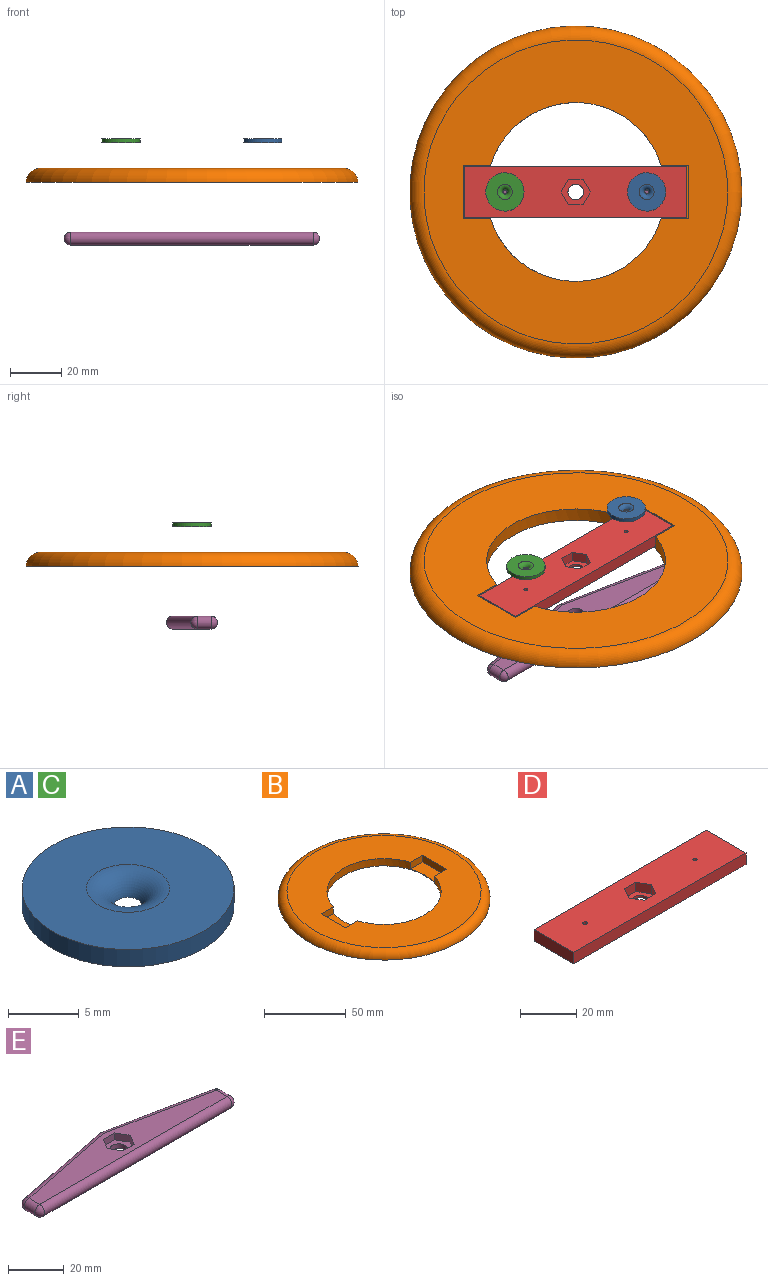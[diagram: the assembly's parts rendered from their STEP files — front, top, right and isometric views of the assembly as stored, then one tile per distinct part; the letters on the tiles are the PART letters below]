
ASSEMBLY  parts=5 mates=4
PART A: 4 faces, bbox 15x15x2 mm
  f0: cylinder r=7.5mm len=15mm, axis (0,0,-1), area 70.7mm2, adj f1,f2
  f1: plane 15x15mm, normal (0,0,1), area 149.6mm2, adj f0,f3
  f2: plane 15x15mm, normal (0,0,-1), area 173.6mm2, adj f0,f3
  f3: torus R=2.94mm, axis (0,0,1), area 29.8mm2, adj f1,f2
PART B: 12 faces, bbox 140.7x140.7x5.5 mm
  f0: plane 21x5mm, normal (1,0,0), area 105mm2, adj f1,f6,f7,f11
  f1: plane 10.61x5mm, normal (0,-1,0), area 53.1mm2, adj f0,f5,f7,f11
  f2: plane 10.61x5mm, normal (0,-1,0), area 53.1mm2, adj f3,f5,f7,f10
  f3: plane 21x5mm, normal (-1,0,0), area 105mm2, adj f2,f4,f7,f10
  f4: plane 10.61x5mm, normal (0,1,0), area 53.1mm2, adj f3,f5,f7,f10
  f5: cylinder r=35mm len=70mm, axis (0,0,-1), area 996.2mm2, adj f1,f2,f4,f6,f7,f8,f10,f11
  f6: plane 10.61x5mm, normal (0,1,0), area 53.1mm2, adj f0,f5,f7,f11
  f7: plane 119x119mm, normal (0,0,1), area 6873.2mm2, adj f0,f1,f2,f3,f4,f5,f6,f9
  f8: plane 130x130mm, normal (0,0,-1), area 9424.8mm2, adj f5,f9
  f9: torus R=59.5mm, axis (0,0,1), area 3419.9mm2, adj f7,f8
  f10: plane 21x10.61mm, normal (0,0,1), area 200.2mm2, adj f2,f3,f4,f5
  f11: plane 21x10.61mm, normal (0,0,1), area 200.2mm2, adj f0,f1,f5,f6
PART C: same geometry as A
PART D: 16 faces, bbox 87x20x5 mm
  f0: plane 87x5mm, normal (0,1,0), area 435mm2, adj f1,f11,f12,f13
  f1: plane 20x5mm, normal (-1,0,0), area 100mm2, adj f0,f2,f12,f13
  f2: plane 87x5mm, normal (0,-1,0), area 435mm2, adj f1,f11,f12,f13
  f3: plane 5x4mm, normal (-0.87,-0.5,0), area 23.1mm2, adj f4,f10,f12,f15
  f4: plane 5x4mm, normal (-0.87,0.5,0), area 23.1mm2, adj f3,f5,f12,f15
  f5: plane 5.77x4mm, normal (0,1,0), area 23.1mm2, adj f4,f6,f12,f15
  f6: plane 5x4mm, normal (0.87,0.5,0), area 23.1mm2, adj f5,f7,f12,f15
  f7: plane 5x4mm, normal (0.87,-0.5,0), area 23.1mm2, adj f6,f10,f12,f15
  f8: cylinder r=0.75mm len=5mm, axis (0,0,-1), area 23.6mm2, adj f12,f13
  f9: cylinder r=0.75mm len=5mm, axis (0,0,-1), area 23.6mm2, adj f12,f13
  f10: plane 5.77x4mm, normal (0,-1,0), area 23.1mm2, adj f3,f7,f12,f15
  f11: plane 20x5mm, normal (1,0,0), area 100mm2, adj f0,f2,f12,f13
  f12: plane 87x20mm, normal (0,0,1), area 1649.9mm2, adj f0,f1,f2,f3,f4,f5,f6,f7
  f13: plane 87x20mm, normal (0,0,-1), area 1707.2mm2, adj f0,f1,f2,f8,f9,f11,f14
  f14: cylinder r=3.05mm len=6.1mm, axis (0,0,-1), area 19.2mm2, adj f13,f15
  f15: plane 11.55x10mm, normal (0,0,1), area 57.4mm2, adj f3,f4,f5,f6,f7,f10,f14
PART E: 20 faces, bbox 100x20x5 mm
  f0: plane 5x3mm, normal (0.87,0.5,0), area 17.3mm2, adj f1,f5,f6,f9
  f1: plane 5x3mm, normal (0.87,-0.5,0), area 17.3mm2, adj f0,f2,f6,f9
  f2: plane 5.77x3mm, normal (0,-1,0), area 17.3mm2, adj f1,f3,f6,f9
  f3: plane 5x3mm, normal (-0.87,-0.5,0), area 17.3mm2, adj f2,f4,f6,f9
  f4: plane 5x3mm, normal (-0.87,0.5,0), area 17.3mm2, adj f3,f5,f6,f9
  f5: plane 5.77x3mm, normal (0,1,0), area 17.3mm2, adj f0,f4,f6,f9
  f6: plane 95x14.95mm, normal (0,0,1), area 882.4mm2, adj f0,f1,f2,f3,f4,f5,f10,f13
  f7: plane 95x14.95mm, normal (0,0,-1), area 939.8mm2, adj f8,f10,f13,f14,f17,f18
  f8: cylinder r=3.05mm len=6.1mm, axis (0,0,-1), area 38.3mm2, adj f7,f9
  f9: plane 11.55x10mm, normal (0,0,1), area 57.4mm2, adj f0,f1,f2,f3,f4,f5,f8
  f10: cylinder r=2.5mm len=95mm, axis (-1,0,0), area 746.1mm2, adj f6,f7,f11,f12
  f11: sphere r=2.5mm, area 19.6mm2, adj f10,f13
  f12: sphere r=2.5mm, area 19.6mm2, adj f10,f14
  f13: cylinder r=2.5mm len=5.45mm, axis (0,-1,0), area 42.8mm2, adj f6,f7,f11,f15
  f14: cylinder r=2.5mm len=5.45mm, axis (0,1,0), area 42.8mm2, adj f6,f7,f12,f16
  f15: sphere r=2.5mm, area 17.2mm2, adj f13,f17
  f16: sphere r=2.5mm, area 17.2mm2, adj f14,f18
  f17: cylinder r=2.5mm len=47.99mm, axis (0.98,-0.2,0), area 380.5mm2, adj f6,f7,f15,f19
  f18: cylinder r=2.5mm len=47.99mm, axis (0.98,0.2,0), area 380.5mm2, adj f6,f7,f16,f19
  f19: sphere r=2.5mm, area 4.9mm2, adj f17,f18
PLACE A t=(36.08,-10.66,-10.48)mm
PLACE B t=(8.36,-10.66,-25.98)mm
PLACE C t=(-19.42,-10.66,-10.48)mm
PLACE D t=(8.69,76.96,-25.48)mm
PLACE E rot(axis=(0,1,0),180deg) t=(5.66,-97.84,-45.48)mm
MATE slider D.f14 <-> B.f11  axis (0,0,-1) through (8.33,-10.66,-25.48)mm
MATE fastened E.f8 <-> D.f14  axis (0,0,1) through (8.33,-10.66,-45.48)mm
MATE fastened A.f3 <-> D.f8  axis (0,0,-1) through (36.08,-10.66,-10.48)mm
MATE fastened C.f0 <-> D.f9  axis (0,0,-1) through (-19.42,-10.66,-10.48)mm
